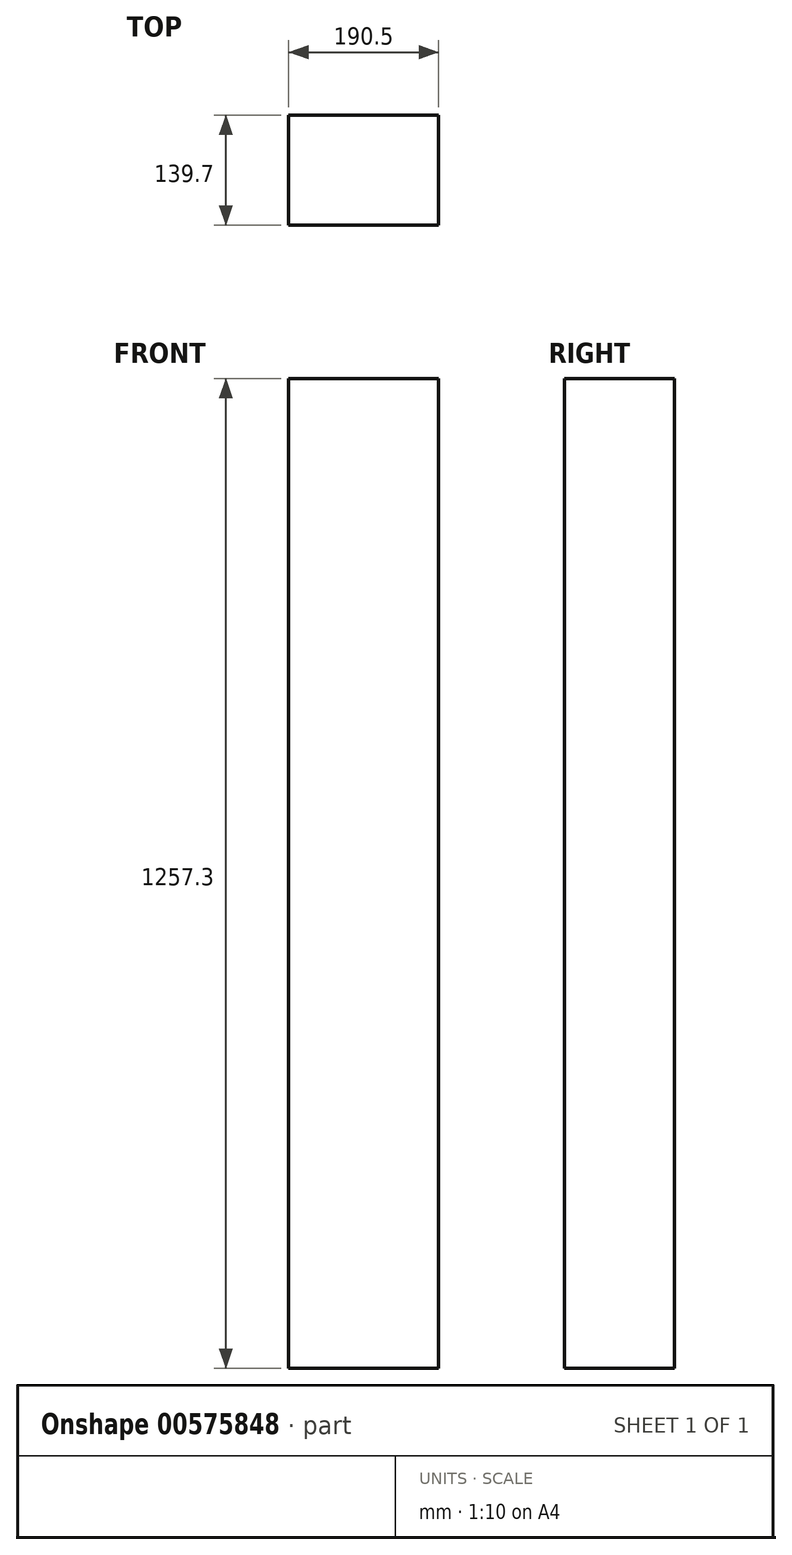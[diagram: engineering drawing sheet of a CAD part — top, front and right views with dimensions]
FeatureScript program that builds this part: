
annotation { "Feature Type Name" : "Feature", "Feature Type Description" : "" }
export const myFeature = defineFeature(function(context is Context, id is Id, definition is map)
    precondition{}
    {
        {
            var Q0;
            Q0=qCreatedBy(makeId("Top.planeOp"),FACE);
            var sketch = newSketch(context, id + "F0", { "sketchPlane" : qUnion([Q0])});
            skLineSegment(sketch, "E0.bottom", {"start": v(0, 0) * mm, "end": v(190.5, 0) * mm});
            skLineSegment(sketch, "E0.top", {"start": v(0, 139.7) * mm, "end": v(190.5, 139.7) * mm});
            skLineSegment(sketch, "E0.left", {"start": v(0, 0) * mm, "end": v(0, 139.7) * mm});
            skLineSegment(sketch, "E0.right", {"start": v(190.5, 0) * mm, "end": v(190.5, 139.7) * mm});
            skSolve(sketch);
        }
        {
            var Q0;
            Q0=qSketchRegion(id+"F0",true);
            extrude(context, id + "F1", {"entities" : qUnion([Q0]), "depth" : 1257.3 * mm, "offsetDistance" : 25.4 * mm});
        }
    });
